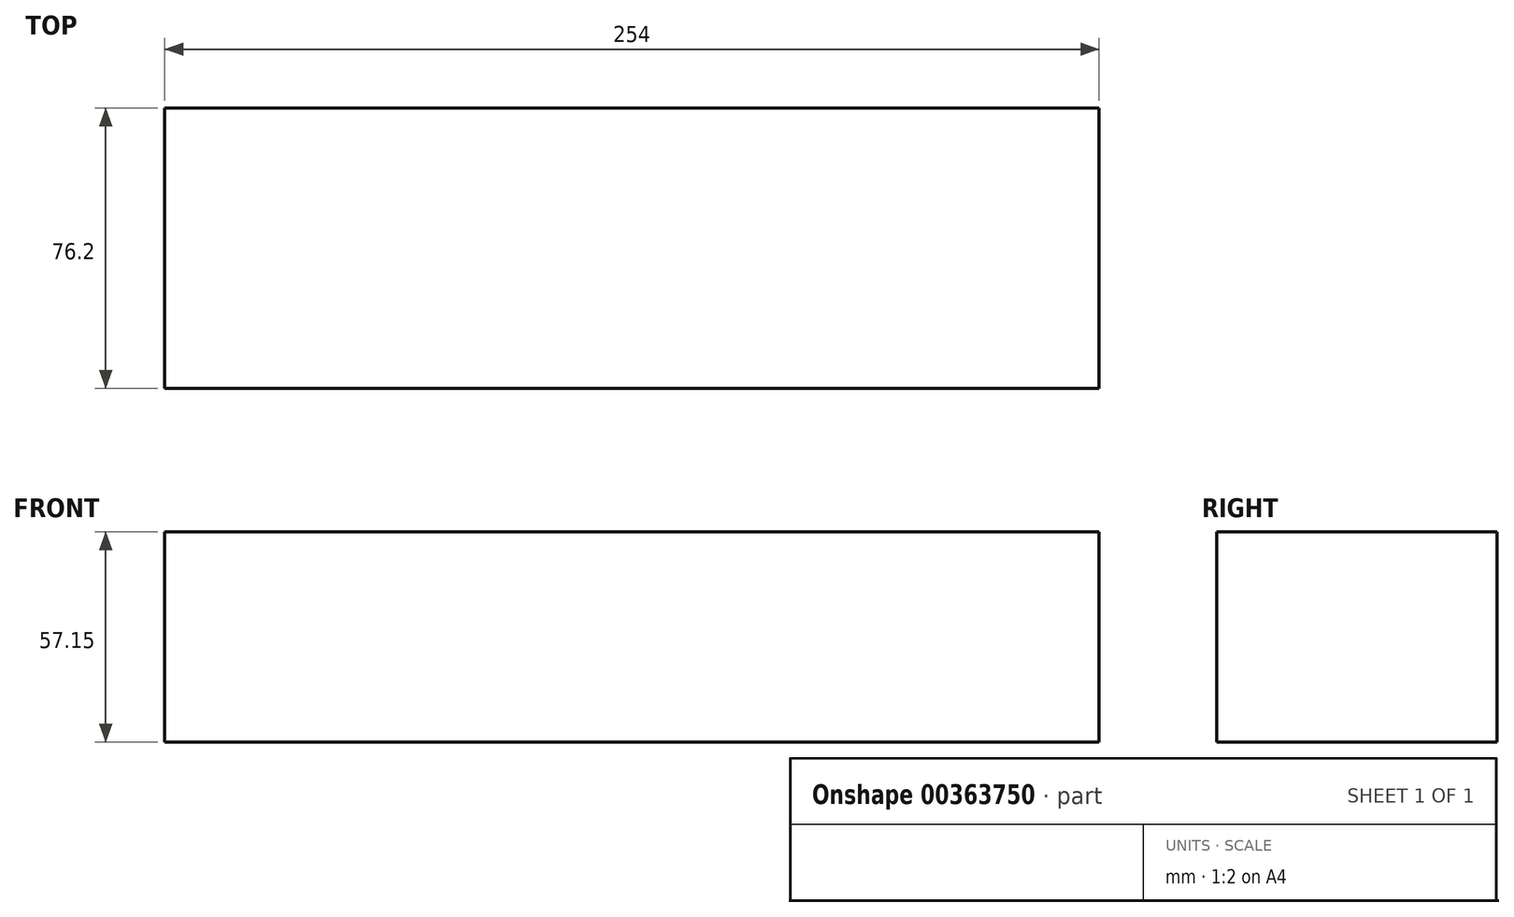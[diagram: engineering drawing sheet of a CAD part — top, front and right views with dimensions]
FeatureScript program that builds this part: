
annotation { "Feature Type Name" : "Feature", "Feature Type Description" : "" }
export const myFeature = defineFeature(function(context is Context, id is Id, definition is map)
    precondition{}
    {
        {
            var Q0;
            Q0=qCreatedBy(makeId("Top.planeOp"),FACE);
            var sketch = newSketch(context, id + "F0", { "sketchPlane" : qUnion([Q0])});
            skLineSegment(sketch, "E0.bottom", {"start": v(127, -38.1) * mm, "end": v(-127, -38.1) * mm});
            skLineSegment(sketch, "E0.top", {"start": v(127, 38.1) * mm, "end": v(-127, 38.1) * mm});
            skLineSegment(sketch, "E0.left", {"start": v(127, -38.1) * mm, "end": v(127, 38.1) * mm});
            skLineSegment(sketch, "E0.right", {"start": v(-127, -38.1) * mm, "end": v(-127, 38.1) * mm});
            skPoint(sketch, "E0.middle", {"position": v(0, 0) * mm});
            skSolve(sketch);
        }
        {
            var Q0;
            Q0 = qSketchRegion(id + "F0", true);
            extrude(context, id + "F1", {"entities" : qUnion([Q0]), "depth" : 57.15 * mm});
        }
    });
